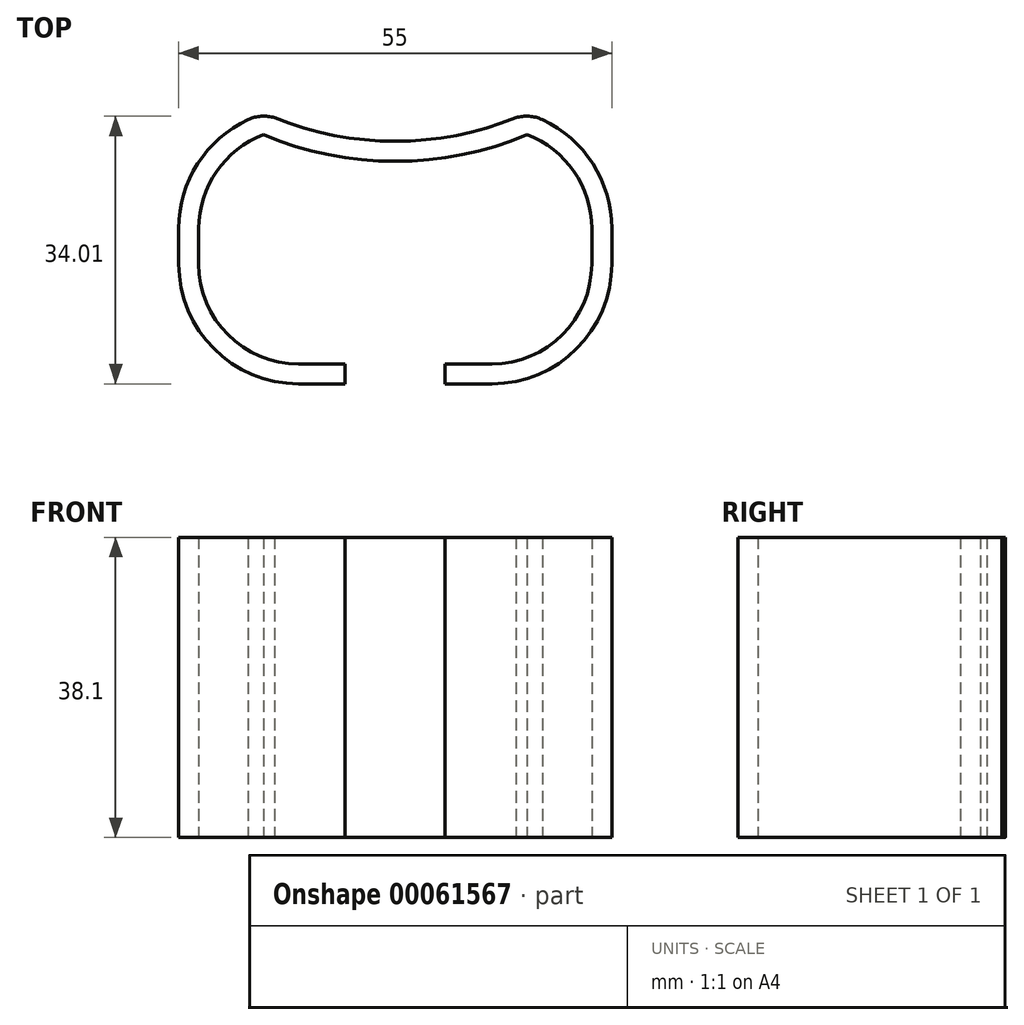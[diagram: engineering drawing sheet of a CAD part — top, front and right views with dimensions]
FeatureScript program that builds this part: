
annotation { "Feature Type Name" : "Feature", "Feature Type Description" : "" }
export const myFeature = defineFeature(function(context is Context, id is Id, definition is map)
    precondition{}
    {
        {
            var Q0;
            Q0=qCreatedBy(makeId("Top.planeOp"),FACE);
            var sketch = newSketch(context, id + "F0", { "sketchPlane" : qUnion([Q0])});
            skLineSegment(sketch, "E0.top", {"start": v(-20.48, -14.9) * mm, "end": v(-14.57, -14.9) * mm});
            skLineSegment(sketch, "E0.left", {"start": v(-35.72, 4.85) * mm, "end": v(-35.72, 0.33) * mm});
            skLineSegment(sketch, "E0.right", {"start": v(19.28, 4.85) * mm, "end": v(19.28, 0.33) * mm});
            skPoint(sketch, "E1.visualSharp", {"position": v(-35.72, 20.1) * mm});
            skArc(sketch, "E1.filletArc", {"start": v(-26.9, 18.68) * mm, "mid": v(-33.33, 13.05) * mm, "end": v(-35.72, 4.85) * mm});
            skPoint(sketch, "E2.visualSharp", {"position": v(-35.72, -14.9) * mm});
            skArc(sketch, "E2.filletArc", {"start": v(-35.72, 0.33) * mm, "mid": v(-31.26, -10.44) * mm, "end": v(-20.48, -14.9) * mm});
            skPoint(sketch, "E3.visualSharp", {"position": v(19.28, -14.9) * mm});
            skArc(sketch, "E3.filletArc", {"start": v(4.04, -14.9) * mm, "mid": v(14.81, -10.44) * mm, "end": v(19.28, 0.33) * mm});
            skPoint(sketch, "E4.visualSharp", {"position": v(19.28, 20.1) * mm});
            skArc(sketch, "E4.filletArc", {"start": v(19.28, 4.85) * mm, "mid": v(16.88, 13.05) * mm, "end": v(10.45, 18.68) * mm});
            skArc(sketch, "E5.0", {"start": v(-24.96, 16.74) * mm, "mid": v(-30.93, 12.08) * mm, "end": v(-33.18, 4.85) * mm});
            skLineSegment(sketch, "E5.1", {"start": v(-33.18, 4.85) * mm, "end": v(-33.18, 0.33) * mm});
            skArc(sketch, "E5.3", {"start": v(-33.18, 0.33) * mm, "mid": v(-29.46, -8.65) * mm, "end": v(-20.48, -12.37) * mm});
            skArc(sketch, "E5.4", {"start": v(16.74, 4.85) * mm, "mid": v(14.48, 12.08) * mm, "end": v(8.51, 16.74) * mm});
            skLineSegment(sketch, "E5.5", {"start": v(16.74, 4.85) * mm, "end": v(16.74, 0.33) * mm});
            skArc(sketch, "E5.6", {"start": v(4.04, -12.37) * mm, "mid": v(13.02, -8.65) * mm, "end": v(16.74, 0.33) * mm});
            skLineSegment(sketch, "E5.7", {"start": v(-20.48, -12.37) * mm, "end": v(-14.57, -12.37) * mm});
            skLineSegment(sketch, "E6", {"start": v(-8.22, 20.1) * mm, "end": v(-8.22, -24.22) * mm, "construction": true});
            skLineSegment(sketch, "E7.0", {"start": v(-14.57, -12.37) * mm, "end": v(-14.57, -14.9) * mm});
            skLineSegment(sketch, "E8.MirrorCS", {"start": v(-1.87, -12.37) * mm, "end": v(-1.87, -14.9) * mm});
            skPoint(sketch, "E9.orphan", {"position": v(-14.57, -24.22) * mm});
            skPoint(sketch, "E10.orphan", {"position": v(-1.87, -24.22) * mm});
            skLineSegment(sketch, "E11.trimOffspring", {"start": v(-1.87, -14.9) * mm, "end": v(4.04, -14.9) * mm});
            skLineSegment(sketch, "E12.trimOffspring", {"start": v(-1.87, -12.37) * mm, "end": v(4.04, -12.37) * mm});
            skPoint(sketch, "E13.orphan", {"position": v(-8.22, -12.37) * mm});
            skLineSegment(sketch, "E14", {"start": v(-8.22, 0) * mm, "end": v(-32.86, 24.64) * mm, "construction": true});
            skLineSegment(sketch, "E15.MirrorCS", {"start": v(-8.22, 0) * mm, "end": v(16.41, 24.64) * mm, "construction": true});
            skArc(sketch, "E16", {"start": v(-24.96, 16.74) * mm, "mid": v(-8.22, 13.37) * mm, "end": v(8.51, 16.74) * mm});
            skArc(sketch, "E17.0", {"start": v(-23.54, 18.9) * mm, "mid": v(-8.22, 15.9) * mm, "end": v(7.1, 18.9) * mm});
            skArc(sketch, "E18", {"start": v(-23.54, 18.9) * mm, "mid": v(-25.24, 19.1) * mm, "end": v(-26.9, 18.68) * mm});
            skArc(sketch, "E19.MirrorCS", {"start": v(7.1, 18.9) * mm, "mid": v(8.8, 19.1) * mm, "end": v(10.45, 18.68) * mm});
            skSolve(sketch);
        }
        {
            var Q0;
            Q0 = qSketchRegion(id + "F0", true);
            extrude(context, id + "F1", {"entities" : qUnion([Q0]), "depth" : 38.1 * mm});
        }
    });
